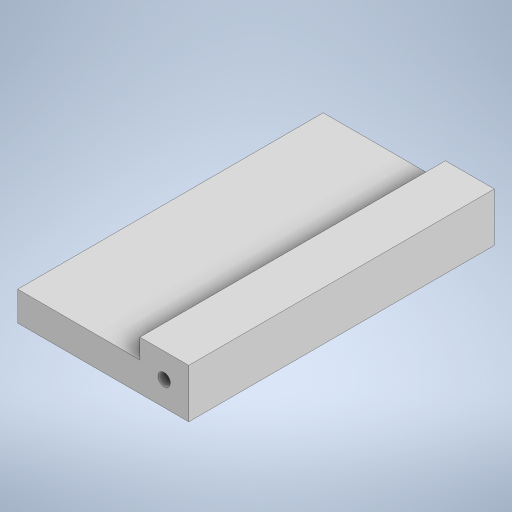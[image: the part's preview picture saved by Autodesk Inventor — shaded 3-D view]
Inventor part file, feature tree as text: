
AUTODESK INVENTOR PART (.ipt)
format: ipt  version: 2023 (Build 270158000, 158)  size: 233,472 bytes
history: native  units: in
note: dims shown in document units (in); Inventor stores cm internally (conversion verified against a paired STEP export)
features: extrude x3, sketch x3
ambient origin geometry x8: Origin, YZ Plane, XZ Plane, XY Plane, X Axis, Y Axis, Z Axis, Center Point
bodies: Body1 (feature_tree)
feature tree (6):
  extrude  "Extrusion2"  Depth=0.7874in
  extrude  "Extrusion3"  Depth=0.3937in
  extrude  "Extrusion4"  Depth=0.9843in TaperAngle=0.0deg
  sketch  "Sketch1"  dims[d0=0.7874in d1=0.7874in]
  sketch  "Sketch3"  dims[d5=0.3937in d6=0.3937in]
  sketch  "Sketch4"  dims[d7=0.1969in d8=0.9843in d9=0.0in d10=0.3543in d11=3.937in d12=0.0in d13=0.4724in d14=1.9685in d15=4.9213in d16=0.0in]
